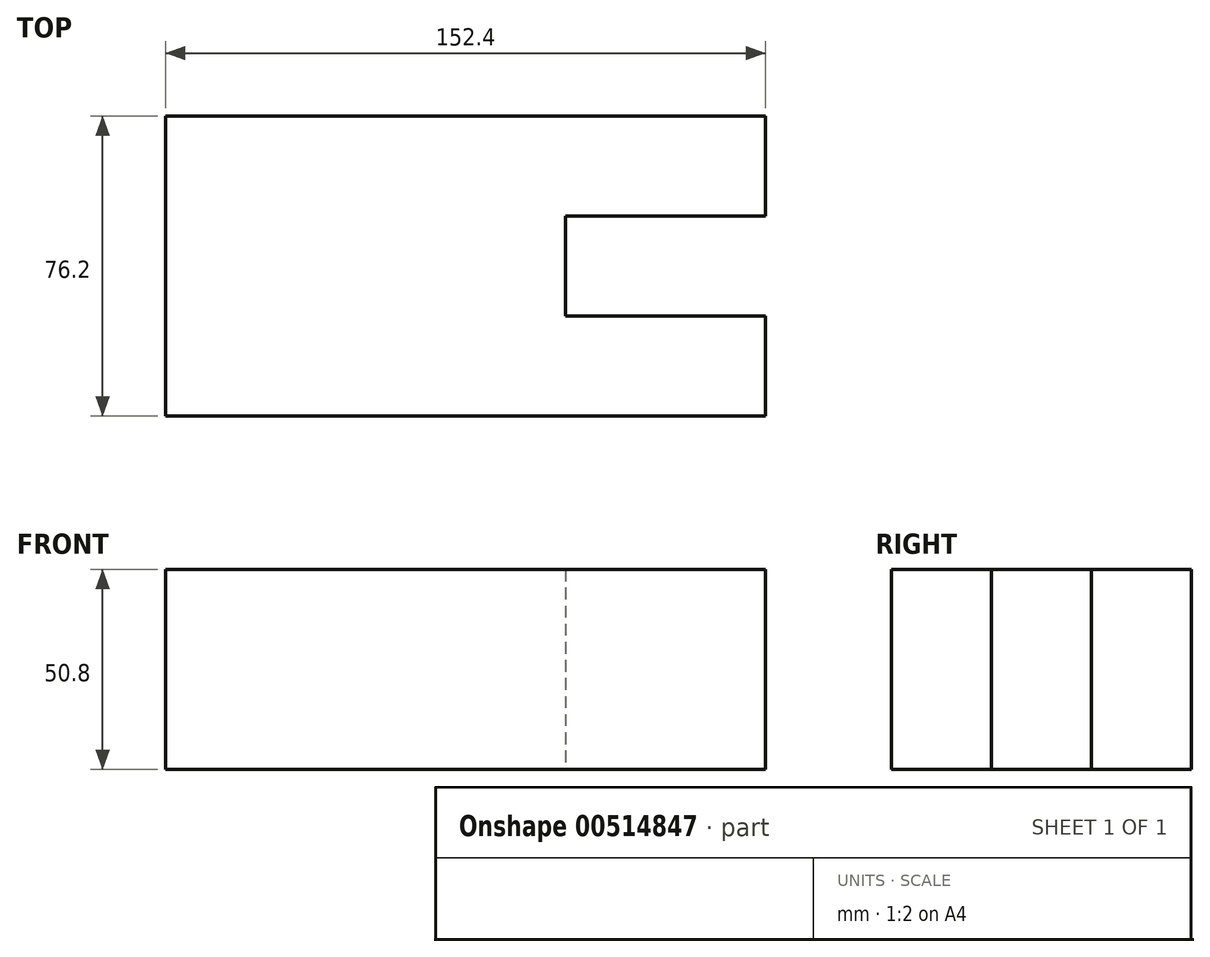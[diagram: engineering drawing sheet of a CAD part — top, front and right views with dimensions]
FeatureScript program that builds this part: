
annotation { "Feature Type Name" : "Feature", "Feature Type Description" : "" }
export const myFeature = defineFeature(function(context is Context, id is Id, definition is map)
    precondition{}
    {
        {
            var Q0;
            Q0=qCreatedBy(makeId("Top.planeOp"),FACE);
            var sketch = newSketch(context, id + "F0", { "sketchPlane" : qUnion([Q0])});
            skLineSegment(sketch, "E0", {"start": v(-71.42, 9.93) * mm, "end": v(-71.42, -66.27) * mm});
            skLineSegment(sketch, "E1", {"start": v(-71.42, -66.27) * mm, "end": v(80.98, -66.27) * mm});
            skLineSegment(sketch, "E2", {"start": v(80.98, -66.27) * mm, "end": v(80.98, -40.87) * mm});
            skLineSegment(sketch, "E3", {"start": v(80.98, -40.87) * mm, "end": v(30.18, -40.87) * mm});
            skLineSegment(sketch, "E4", {"start": v(30.18, -40.87) * mm, "end": v(30.18, -15.47) * mm});
            skLineSegment(sketch, "E5", {"start": v(30.18, -15.47) * mm, "end": v(80.98, -15.47) * mm});
            skLineSegment(sketch, "E6", {"start": v(80.98, -15.47) * mm, "end": v(80.98, 9.93) * mm});
            skLineSegment(sketch, "E7", {"start": v(80.98, 9.93) * mm, "end": v(-71.42, 9.93) * mm});
            skSolve(sketch);
        }
        {
            var Q0;
            Q0 = qSketchRegion(id + "F0", true);
            extrude(context, id + "F1", {"entities" : qUnion([Q0]), "depth" : 50.8 * mm, "offsetDistance" : 25.4 * mm});
        }
    });
